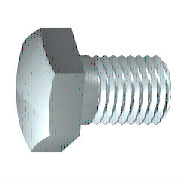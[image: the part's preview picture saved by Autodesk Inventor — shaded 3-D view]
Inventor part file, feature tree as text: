
AUTODESK INVENTOR PART (.ipt)
format: ipt  version: 2025.1 (Build 291241020, 241B)  size: 197,120 bytes
history: native  units: mm (DEFAULTED — no unit token found)
features: extrude x1, chamfer x1, plane x1
ambient origin geometry x7: Origin, YZ Plane, XZ Plane, X Axis, Y Axis, Z Axis, Center Point
bodies: Solid1 (feature_tree), Body (feature_tree)
feature tree (3):
  extrude  "Head"  Depth=40.0mm
  chamfer  "Chamfer1"  Distance=34.7mm
  plane  "Work Plane1"
